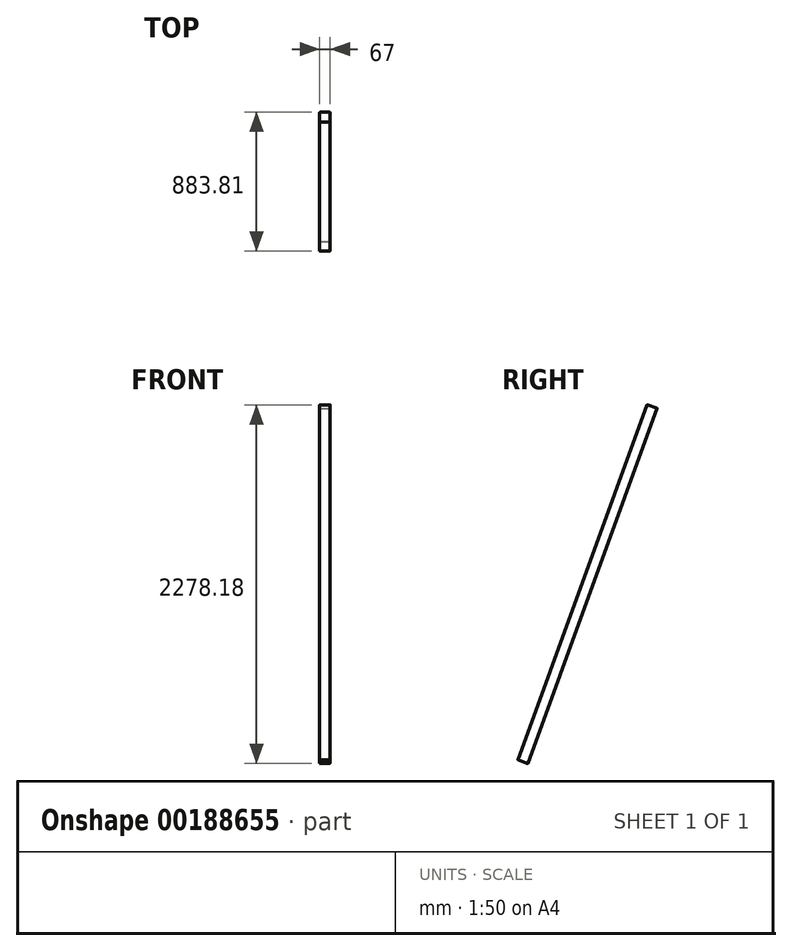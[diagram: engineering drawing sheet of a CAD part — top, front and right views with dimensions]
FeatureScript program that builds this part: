
annotation { "Feature Type Name" : "Feature", "Feature Type Description" : "" }
export const myFeature = defineFeature(function(context is Context, id is Id, definition is map)
    precondition{}
    {
        {
            var Q0;
            Q0=qCreatedBy(makeId("Front.planeOp"),FACE);
            var sketch = newSketch(context, id + "F0", { "sketchPlane" : qUnion([Q0])});
            skLineSegment(sketch, "E0.bottom", {"start": v(-28.5, 33.5) * mm, "end": v(28.5, 33.5) * mm});
            skLineSegment(sketch, "E0.top", {"start": v(-28.5, -33.5) * mm, "end": v(28.5, -33.5) * mm});
            skLineSegment(sketch, "E0.left", {"start": v(-33.5, 28.5) * mm, "end": v(-33.5, -28.5) * mm});
            skLineSegment(sketch, "E0.right", {"start": v(33.5, 28.5) * mm, "end": v(33.5, -28.5) * mm});
            skLineSegment(sketch, "E1", {"start": v(0, 53.32) * mm, "end": v(0, -69.02) * mm, "construction": true});
            skLineSegment(sketch, "E2", {"start": v(-62.16, 0) * mm, "end": v(68.96, 0) * mm, "construction": true});
            skPoint(sketch, "E3.visualSharp", {"position": v(-33.5, 33.5) * mm});
            skArc(sketch, "E3.filletArc", {"start": v(-28.5, 33.5) * mm, "mid": v(-32.04, 32.04) * mm, "end": v(-33.5, 28.5) * mm});
            skPoint(sketch, "E4.visualSharp", {"position": v(33.5, 33.5) * mm});
            skArc(sketch, "E4.filletArc", {"start": v(33.5, 28.5) * mm, "mid": v(32.04, 32.04) * mm, "end": v(28.5, 33.5) * mm});
            skPoint(sketch, "E5.visualSharp", {"position": v(33.5, -33.5) * mm});
            skArc(sketch, "E5.filletArc", {"start": v(28.5, -33.5) * mm, "mid": v(32.04, -32.04) * mm, "end": v(33.5, -28.5) * mm});
            skPoint(sketch, "E6.visualSharp", {"position": v(-33.5, -33.5) * mm});
            skArc(sketch, "E6.filletArc", {"start": v(-33.5, -28.5) * mm, "mid": v(-32.04, -32.04) * mm, "end": v(-28.5, -33.5) * mm});
            skSolve(sketch);
        }
        {
            var Q0;
            Q0=qSketchRegion(id+"F0",true);
            extrude(context, id + "F1", {"entities" : qUnion([Q0]), "depth" : 2400 * mm});
        }
        {
            var Q0;
            Q0=makeQuery(id+"F1.opExtrude","SWEPT_BODY",BODY,{"disambiguationData":[OSD([sQuery(id+"F0.wireOp",EDGE,"E0.bottom"),sQuery(id+"F0.wireOp",EDGE,"E0.top"),sQuery(id+"F0.wireOp",EDGE,"E0.left"),sQuery(id+"F0.wireOp",EDGE,"E0.right"),sQuery(id+"F0.wireOp",EDGE,"E3.filletArc"),sQuery(id+"F0.wireOp",EDGE,"E4.filletArc"),sQuery(id+"F0.wireOp",EDGE,"E5.filletArc"),sQuery(id+"F0.wireOp",EDGE,"E6.filletArc")])]});
            var Q1;
            Q1=sQuery(id+"F0.wireOp",EDGE,"E0.bottom");
            transform(context, id + "F2", {"entities" : qUnion([Q0]), "transformType" : TransformType.ROTATION, "transformAxis" : qUnion([Q1]), "angle" : 110 * degree, "oppositeDirection" : true, "makeCopy" : false});
        }
        {
            var Q0;
            Q0=makeQuery(id+"F1.opExtrude","SWEPT_BODY",BODY,{"disambiguationData":[OSD([sQuery(id+"F0.wireOp",EDGE,"E0.bottom"),sQuery(id+"F0.wireOp",EDGE,"E0.top"),sQuery(id+"F0.wireOp",EDGE,"E0.left"),sQuery(id+"F0.wireOp",EDGE,"E0.right"),sQuery(id+"F0.wireOp",EDGE,"E3.filletArc"),sQuery(id+"F0.wireOp",EDGE,"E4.filletArc"),sQuery(id+"F0.wireOp",EDGE,"E5.filletArc"),sQuery(id+"F0.wireOp",EDGE,"E6.filletArc")])]});
            transform(context, id + "F3", {"entities" : qUnion([Q0]), "transformType" : TransformType.TRANSLATION_3D, "dx" : 0 * mm, "dy" : -320 * mm, "dz" : 0 * mm, "makeCopy" : false});
        }
    });
